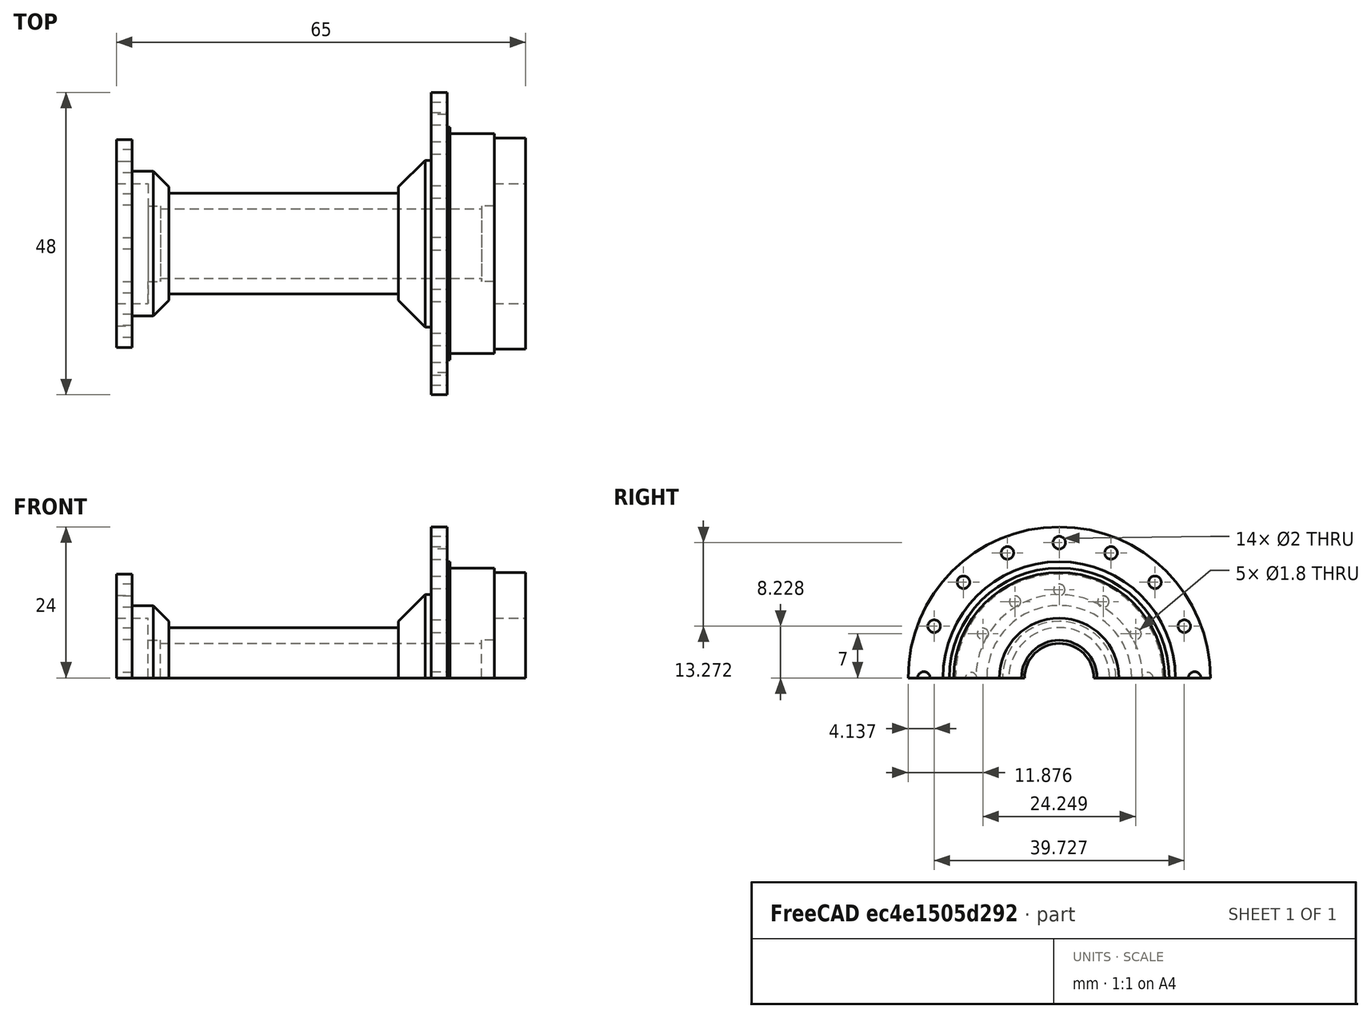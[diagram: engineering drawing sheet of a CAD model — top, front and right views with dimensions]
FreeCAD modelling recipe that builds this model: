
FCSTD DOCUMENT  (FreeCAD 0.16R)
Label: 75mmFixieWaxle
License: All rights reserved
LicenseURL: http://en.wikipedia.org/wiki/All_rights_reserved
objects: Sketcher::SketchObject×3, PartDesign::Pocket×2, PartDesign::PolarPattern×2, PartDesign::Revolution×1, Mesh::Feature×1
note: 11 computed .brp shape members not serialized (recipe doc carries the construction recipe); baked Part::Feature solids carry a one-line shape summary decoded from their .brp

FEATURE [Sketcher::SketchObject] Sketch
  sketch-geometry (28):
    g0: LineSegment StartX=0 StartY=9.2 StartZ=0 EndX=0 EndY=16.76 EndZ=0
    g1: LineSegment StartX=0 StartY=16.76 StartZ=0 EndX=-5 EndY=16.76 EndZ=0
    g2: LineSegment StartX=-5 StartY=16.76 StartZ=0 EndX=-5 EndY=17.46 EndZ=0
    g3: LineSegment StartX=-5 StartY=17.46 StartZ=0 EndX=-12 EndY=17.46 EndZ=0
    g4: LineSegment StartX=-12 StartY=17.46 StartZ=0 EndX=-12 EndY=18.46 EndZ=0
    g5: LineSegment StartX=-12 StartY=18.46 StartZ=0 EndX=-12.5 EndY=18.46 EndZ=0
    g6: LineSegment StartX=-12.5 StartY=18.46 StartZ=0 EndX=-12.5 EndY=24 EndZ=0
    g7: LineSegment StartX=-12.5 StartY=24 StartZ=0 EndX=-15 EndY=24 EndZ=0
    g8: LineSegment StartX=-15 StartY=24 StartZ=0 EndX=-15 EndY=13.2426 EndZ=0
    g9: LineSegment StartX=-15 StartY=13.2426 StartZ=0 EndX=-16 EndY=13.2426 EndZ=0
    g10: LineSegment StartX=-16 StartY=13.2426 StartZ=0 EndX=-20.2426 EndY=9 EndZ=0
    g11: LineSegment StartX=-20.2426 StartY=9 StartZ=0 EndX=-20.2426 EndY=8 EndZ=0
    g12: LineSegment StartX=-20.2426 StartY=8 StartZ=0 EndX=-56.6716 EndY=8 EndZ=0
    g13: LineSegment StartX=-56.6716 StartY=8 StartZ=0 EndX=-56.6716 EndY=9 EndZ=0
    g14: LineSegment StartX=-56.6716 StartY=9 StartZ=0 EndX=-59.1716 EndY=11.5 EndZ=0
    g15: LineSegment StartX=-59.1716 StartY=11.5 StartZ=0 EndX=-62.5 EndY=11.5 EndZ=0
    g16: LineSegment StartX=-62.5 StartY=11.5 StartZ=0 EndX=-62.5 EndY=16.5 EndZ=0
    g17: LineSegment StartX=-62.5 StartY=16.5 StartZ=0 EndX=-65 EndY=16.5 EndZ=0
    g18: LineSegment StartX=-65 StartY=16.5 StartZ=0 EndX=-65 EndY=9.2 EndZ=0
    g19: LineSegment StartX=-65 StartY=9.2 StartZ=0 EndX=-70 EndY=9.2 EndZ=0
    g20: LineSegment StartX=-70 StartY=9.2 StartZ=0 EndX=-70 EndY=7.6 EndZ=0
    g21: LineSegment StartX=-70 StartY=7.6 StartZ=0 EndX=-71 EndY=7.6 EndZ=0
    g22: LineSegment StartX=-71 StartY=7.6 StartZ=0 EndX=-71 EndY=2.6 EndZ=0
    g23: LineSegment StartX=-71 StartY=2.6 StartZ=0 EndX=6 EndY=2.6 EndZ=0
    g24: LineSegment StartX=6 StartY=2.6 StartZ=0 EndX=6 EndY=7.6 EndZ=0
    g25: LineSegment StartX=6 StartY=7.6 StartZ=0 EndX=5 EndY=7.6 EndZ=0
    g26: LineSegment StartX=5 StartY=7.6 StartZ=0 EndX=5 EndY=9.2 EndZ=0
    g27: LineSegment StartX=5 StartY=9.2 StartZ=0 EndX=0 EndY=9.2 EndZ=0
  constraints (81):
    c: Coincident(g0,g1)
    c: Horizontal(g1)
    c: Coincident(g1,g2)
    c: Coincident(g2,g3)
    c: Coincident(g3,g4)
    c: Coincident(g4,g5)
    c: Coincident(g5,g6)
    c: Vertical(g6)
    c: Coincident(g6,g7)
    c: Horizontal(g7)
    c: Coincident(g7,g8)
    c: Vertical(g8)
    c: Coincident(g8,g9)
    c: Coincident(g9,g10)
    c: Coincident(g10,g11)
    c: Vertical(g11)
    c: Coincident(g11,g12)
    c: Horizontal(g12)
    c: Coincident(g12,g13)
    c: Vertical(g13)
    c: Coincident(g13,g14)
    c: Coincident(g14,g15)
    c: Horizontal(g15)
    c: Coincident(g15,g16)
    c: Vertical(g16)
    c: Coincident(g16,g17)
    c: Coincident(g17,g18)
    c: Vertical(g18)
    c: Horizontal(g9)
    c: Horizontal(g3)
    c: Horizontal(g17)
    c: DistanceX(g18,g0) = 65
    c: Vertical(g0)
    c: DistanceX(g5,g5) = 0.5
    c: Horizontal(g5)
    c: Vertical(g4)
    c: DistanceY(g-1,g2) = 17.46
    c: Vertical(g2)
    c: DistanceX(g7,g7) = 2.5
    c: DistanceX(g3,g3) = 7
    c: DistanceX(g1,g1) = 5
    c: DistanceY(g4,g4) = 1
    c: DistanceY(g-1,g11) = 8
    c: DistanceX(g17,g17) = 2.5
    c: DistanceY(g-1,g7) = 24
    c: Distance(g11) = 1
    c: Distance(g9) = 1
    c: Angle(g14) = 2.35619
    c: Angle(g10) = -2.35619
    c: Distance(g10) = 6
    c: DistanceX(g-1,g0) = 0
    c: DistanceY(g16,g16) = 5
    c: Distance(g13) = 1
    c: Horizontal(g19)
    c: Coincident(g19,g20)
    c: Vertical(g20)
    c: Coincident(g20,g21)
    c: Horizontal(g21)
    c: Coincident(g21,g22)
    c: Vertical(g22)
    c: Coincident(g22,g23)
    c: Horizontal(g23)
    c: Coincident(g23,g24)
    c: Vertical(g24)
    c: Coincident(g24,g25)
    c: Coincident(g25,g26)
    c: Coincident(g26,g27)
    c: Horizontal(g27)
    c: Horizontal(g25)
    c: Vertical(g26)
    c: Distance(g22) = 5
    c: Distance(g19,g23) = 6.6
    c: Coincident(g18,g19)
    c: Distance(g24,g23) = 5
    c: Distance(g26,g23) = 6.6
    c: DistanceX(g27,g27) = 5
    c: Coincident(g27,g0)
    c: DistanceX(g25,g25) = 1
    c: DistanceX(g21,g21) = 1
    c: DistanceX(g19,g19) = 5
    c: DistanceY(g-1,g22) = 2.6
FEATURE [PartDesign::Revolution] Revolution
  Angle = 180
  Axis = (1,0,0)
  Base = (0,0,0)
  ReferenceAxis = -> Sketch [H_Axis]
  Sketch = -> Sketch
FEATURE [Sketcher::SketchObject] Sketch001
  ExternalGeometry = -> [Revolution]
  Placement = pos=(-12.5,0,0) rot=(0.57735,0.57735,0.57735;2.0944rad)
  Support = -> Revolution [Face9]
  sketch-geometry (1):
    g0: Circle CenterX=-21.5 CenterY=0 CenterZ=0 NormalX=0 NormalY=0 NormalZ=1 Radius=1
  constraints (3):
    c: Radius(g0) = 1
    c: PointOnObject(g0,g-1)
    c: Distance(g0,g-3) = 2.5
FEATURE [PartDesign::Pocket] Pocket
  Length = 5
  Sketch = -> Sketch001
  Type = 0
FEATURE [PartDesign::PolarPattern] PolarPattern
  Angle = 180
  Axis = -> Sketch001 [N_Axis]
  Occurrences = 9
  Originals = -> [Pocket]
  Reversed = true
FEATURE [Sketcher::SketchObject] Sketch002
  ExternalGeometry = -> [PolarPattern]
  Placement = pos=(-65,0,0) rot=(0.57735,-0.57735,-0.57735;2.0944rad)
  Support = -> PolarPattern [Face13]
  sketch-geometry (1):
    g0: Circle CenterX=-14 CenterY=0 CenterZ=0 NormalX=0 NormalY=0 NormalZ=1 Radius=0.9
  constraints (3):
    c: Radius(g0) = 0.9
    c: PointOnObject(g0,g-1)
    c: DistanceX(g-3,g0) = 2.5
FEATURE [PartDesign::Pocket] Pocket001
  Length = 5
  Sketch = -> Sketch002
  Type = 0
FEATURE [PartDesign::PolarPattern] PolarPattern001
  Angle = 180
  Axis = -> Sketch002 [N_Axis]
  Occurrences = 7
  Originals = -> [Pocket001]
  Reversed = true
FEATURE [Mesh::Feature] Mesh  label="PolarPattern001 (Meshed)"
